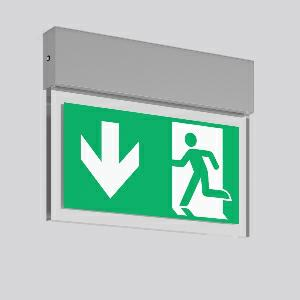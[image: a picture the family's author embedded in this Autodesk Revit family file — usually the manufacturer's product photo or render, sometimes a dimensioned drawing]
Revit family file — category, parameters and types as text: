
# Revit family: halyxx_671737_004_1_a562
name_source: partatom
category: Lighting Fixtures
units: mm (PartAtom-declared; Revit-internal decimal feet)

## family parameters
Cut with Voids When Loaded = No
Host = Face
Light Source = No
Part Type = Normal
Room Calculation Point = No
Round Connector Dimension = Use Diameter
Shared = No

## types (1)
- HALYXX (1 x LED Modul 840, 90 lm, 4000)
    Apparent Load = 3 VA
    Approval mark = CE
    CIE Flux Codes = 18 45 74 52 100
    Color Rendering = 80
    Color Temperature = 4000
    Default Elevation = 1800 mm
    Description = Series: HALYXX
Luminaire for escape route identification. Housing: extruded aluminium profile, anodised or powder-coated. Display panel: highly transparent panel, plastic, with legend on one side/both sides. Driver integrated. Suitable for connection to central battery systems. Please indicate legend number when placing your order! 
Colour: anodised aluminium
Length: 340 mm
Width: 40 mm
Height: 270 mm
Weight: 2.01 kg
Operating mode: maintained power mode
Viewing Distance: 30 m
Lamp: LED
Socket: without socket
Colour temperature: 4000K
Colour rendering index (CRI): 80
System power: 3.1 W
Rated luminous flux: 90 lm
Luminous flux, emergency: 90
System power, emergency: 2.9 W
Control gear: Regulated power supply
Protection class: I
Type of protection: IP 40
    Height = 270 mm
    Lamp = 1 x LED Modul 840
    Lamp Light Flux = 90 lm
    Lamp count = 1
    Length = 340 mm
    Lifetime = 50000 h
    Luminous efficacy = 29 lm/W
    Manufacturer = RZB
    ModVariant = No
    Model = 671737.004.1
    Mounting Place = Ceiling
    Mounting Type = Surface mounted
    Number of Poles = 1
    OnlyDefault = Yes
    Power Factor = 1
    Product Name = HALYXX
    Product group = Surface mounted ceiling luminaires
    ProductGroupID = 303
    Protection Class = Protection class I
    Protection Degree = IP 40
    RLX_Detail_Level = 1
    RLX_Emergency_Light_Flux = 90 lm
    RLX_Emergency_Type = 3
    RLX_Emergency_Type_DB = Yes
    RlxData = <blob elided: 54921 chars, md5=973c5cdf>
    Socket = socket
    Standby Power = 0 W
    System Light Flux = 90 lm
    System Power = 3 W
    Type Comments = Product without accessories
    Type Image = 671744.004.jpg
    URL = http://relux.com
    VarID = ---
    Voltage = 230 V
    Voltage Range = 220-240 V
    Weight = 0.00 kg
    Width = 40 mm  [stored 0.131234 ft]

note: [stored X ft] marks values corroborated as IEEE doubles in the binary element streams (Revit-internal decimal feet)

## geometry (parser evidence)
native form markers: Blend x4, Sweep x16
no freeform markers — native parametric forms only
